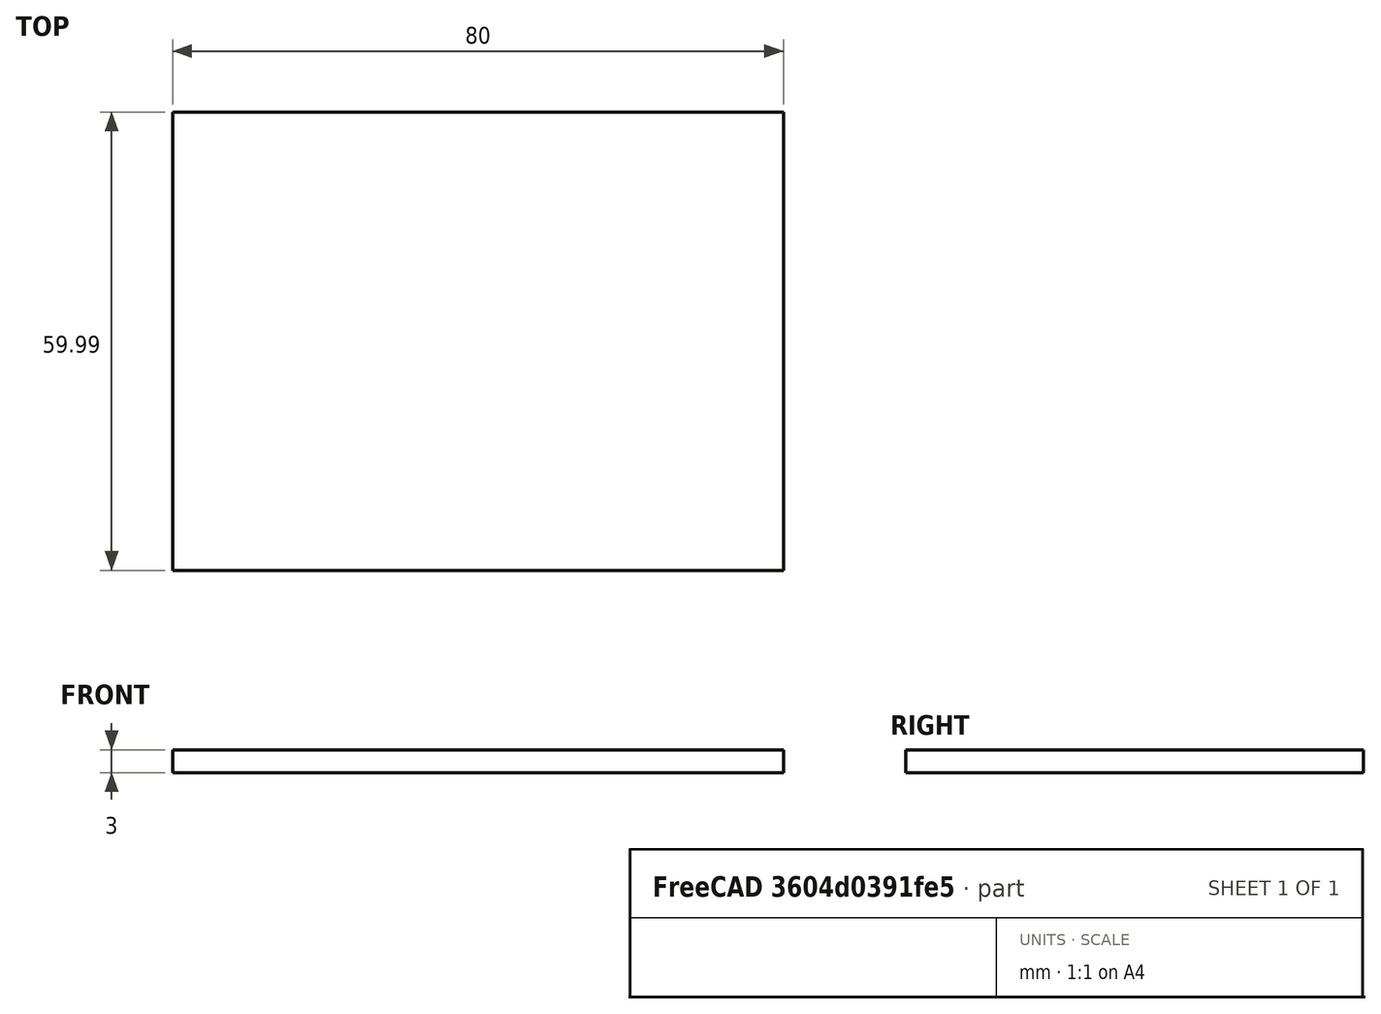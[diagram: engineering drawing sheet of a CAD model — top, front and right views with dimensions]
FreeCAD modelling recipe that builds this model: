
FCSTD DOCUMENT  (FreeCAD 0.19R24291 (Git))
Label: protoboard
License: All rights reserved
LicenseURL: http://en.wikipedia.org/wiki/All_rights_reserved
objects: Sketcher::SketchObject×1, PartDesign::Pad×1, PartDesign::Body×1
note: 4 computed .brp shape members not serialized (recipe doc carries the construction recipe); baked Part::Feature solids carry a one-line shape summary decoded from their .brp

FEATURE [Sketcher::SketchObject] Sketch
  FullyConstrained = false
  MapMode = 5
  Support = -> [XY_Plane]
  sketch-geometry (4):
    g0: LineSegment StartX=-46.7569 StartY=40.5161 StartZ=0 EndX=33.2431 EndY=40.5161 EndZ=0
    g1: LineSegment StartX=33.2431 StartY=40.5161 StartZ=0 EndX=33.2431 EndY=-19.4739 EndZ=0
    g2: LineSegment StartX=33.2431 StartY=-19.4739 StartZ=0 EndX=-46.7569 EndY=-19.4739 EndZ=0
    g3: LineSegment StartX=-46.7569 StartY=-19.4739 StartZ=0 EndX=-46.7569 EndY=40.5161 EndZ=0
  constraints (10):
    c: Coincident(g0,g1)
    c: Coincident(g1,g2)
    c: Coincident(g2,g3)
    c: Coincident(g3,g0)
    c: Horizontal(g0)
    c: Horizontal(g2)
    c: Vertical(g1)
    c: Vertical(g3)
    c: DistanceX(g0,g0) = 80
    c: DistanceY(g1,g1) = 59.99
FEATURE [PartDesign::Pad] Pad
  Direction = (1,1,1)
  Length = 3
  Length2 = 100
  Profile = -> Sketch
  Type = 0
FEATURE [PartDesign::Body] Body
  Group = -> [Sketch,Pad]
  Origin = -> Origin
  Tip = -> Pad
